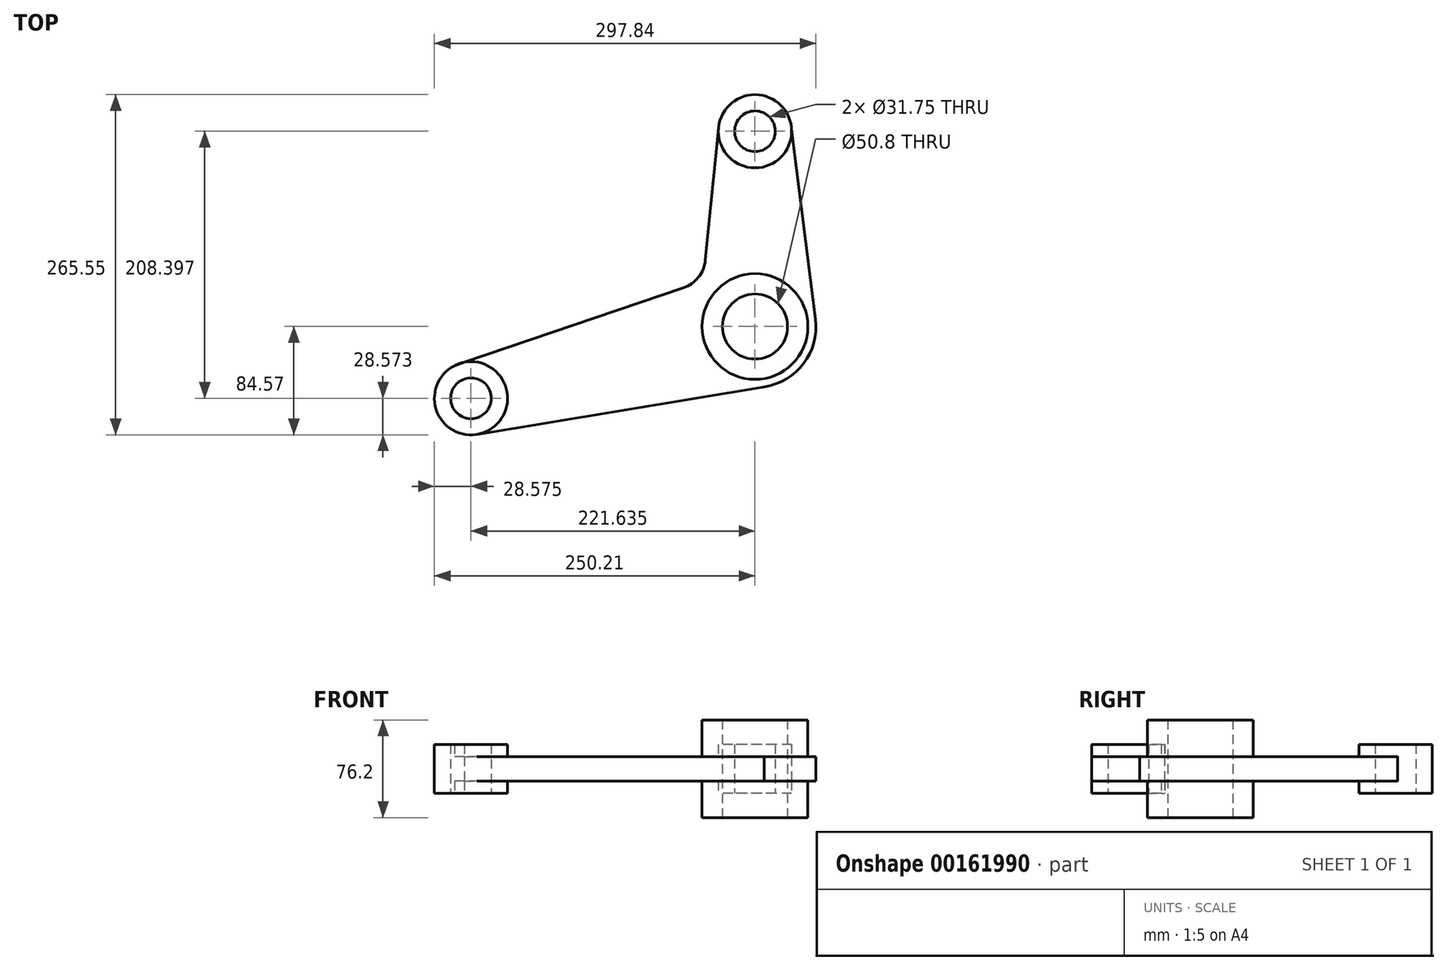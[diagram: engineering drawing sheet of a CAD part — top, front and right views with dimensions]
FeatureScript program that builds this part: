
annotation { "Feature Type Name" : "Feature", "Feature Type Description" : "" }
export const myFeature = defineFeature(function(context is Context, id is Id, definition is map)
    precondition{}
    {
        {
            var Q0;
            Q0=qCreatedBy(makeId("Top.planeOp"),FACE);
            var sketch = newSketch(context, id + "F0", { "sketchPlane" : qUnion([Q0])});
            skCircle(sketch, "E0", {"center": v(0, 0) * mm, "radius": 41.28 * mm});
            skCircle(sketch, "E1", {"center": v(0, 0) * mm, "radius": 25.4 * mm});
            skCircle(sketch, "E2", {"center": v(0, 152.4) * mm, "radius": 28.58 * mm});
            skCircle(sketch, "E3", {"center": v(-221.64, -56) * mm, "radius": 28.58 * mm});
            skArc(sketch, "E4", {"start": v(7.06, -47.1) * mm, "mid": v(37.97, -28.75) * mm, "end": v(47.25, 5.97) * mm});
            skCircle(sketch, "E5", {"center": v(-221.64, -56) * mm, "radius": 15.88 * mm});
            skCircle(sketch, "E6", {"center": v(0, 152.4) * mm, "radius": 15.88 * mm});
            skLineSegment(sketch, "E7", {"start": v(-234.52, -30.5) * mm, "end": v(-55.83, 30.25) * mm});
            skLineSegment(sketch, "E8", {"start": v(-38.73, 51.78) * mm, "end": v(-28.43, 155.23) * mm});
            skPoint(sketch, "E9.visualSharp", {"position": v(-40.35, 35.5) * mm});
            skArc(sketch, "E9.filletArc", {"start": v(-55.83, 30.25) * mm, "mid": v(-44.11, 38.5) * mm, "end": v(-38.73, 51.78) * mm});
            skLineSegment(sketch, "E10", {"start": v(28.52, 154.12) * mm, "end": v(47.25, 5.97) * mm});
            skLineSegment(sketch, "E11", {"start": v(8.5, -46.86) * mm, "end": v(-216.97, -84.19) * mm});
            skSolve(sketch);
        }
        {
            var Q0;
            Q0 = qSketchRegion(id + "F0", true);
            extrude(context, id + "F1", {"entities" : qUnion([Q0]), "endBound" : BoundingType.SYMMETRIC, "depth" : 19.05 * mm});
        }
        {
            var Q0;
            Q0=makeQuery(id+"F0.imprint","IMPRINT",FACE,{"disambiguationData":[TD([[makeQuery(id+"F0.imprint","IMPRINT",EDGE,{"derivedFrom":sQuery(id+"F0.wireOp",EDGE,"E5")}),-1.0]])]});
            var Q1;
            Q1=makeQuery(id+"F0.imprint","IMPRINT",FACE,{"disambiguationData":[TD([[makeQuery(id+"F0.imprint","IMPRINT",EDGE,{"derivedFrom":sQuery(id+"F0.wireOp",EDGE,"E6")}),-1.0]])]});
            var Q2;
            Q2=makeQuery(id+"F0.imprint","IMPRINT",FACE,{"disambiguationData":[TD([[makeQuery(id+"F0.imprint","IMPRINT",EDGE,{"derivedFrom":sQuery(id+"F0.wireOp",EDGE,"E0")}),1.0]])]});
            extrude(context, id + "F2", {"entities" : qUnion([Q0, Q1, Q2]), "operationType" : NewBodyOperationType.ADD, "endBound" : BoundingType.SYMMETRIC, "depth" : 38.1 * mm});
        }
        {
            var Q0;
            Q0=makeQuery(id+"F2.opExtrude","CAP_FACE",FACE,{"disambiguationData":[OSD([sQuery(id+"F0.wireOp",EDGE,"E0"),sQuery(id+"F0.wireOp",EDGE,"E1")])],"isStart":false});
            extrude(context, id + "F3", {"entities" : qUnion([Q0]), "operationType" : NewBodyOperationType.ADD, "depth" : 19.05 * mm});
        }
        {
            var Q0;
            Q0=makeQuery(id+"F2.opExtrude","CAP_FACE",FACE,{"disambiguationData":[OSD([sQuery(id+"F0.wireOp",EDGE,"E0"),sQuery(id+"F0.wireOp",EDGE,"E1")])],"isStart":true});
            extrude(context, id + "F4", {"entities" : qUnion([Q0]), "operationType" : NewBodyOperationType.ADD, "depth" : 19.05 * mm});
        }
    });
